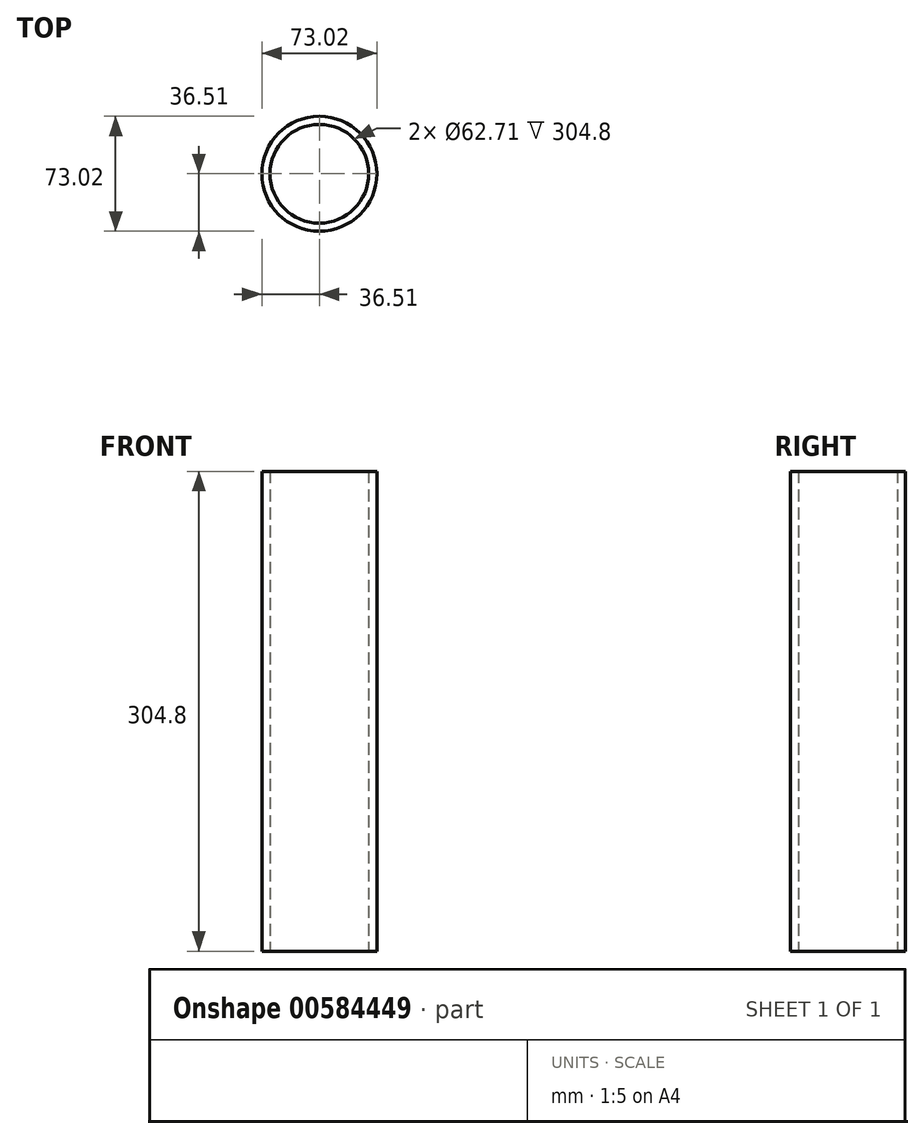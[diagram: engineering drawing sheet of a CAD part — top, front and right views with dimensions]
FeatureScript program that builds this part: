
annotation { "Feature Type Name" : "Feature", "Feature Type Description" : "" }
export const myFeature = defineFeature(function(context is Context, id is Id, definition is map)
    precondition{}
    {
        {
            var Q0;
            Q0=qCreatedBy(makeId("Top.planeOp"),FACE);
            var sketch = newSketch(context, id + "F0", { "sketchPlane" : qUnion([Q0])});
            skCircle(sketch, "E0", {"center": v(0, 0) * mm, "radius": 36.51 * mm});
            skCircle(sketch, "E1", {"center": v(0, 0) * mm, "radius": 31.36 * mm});
            skSolve(sketch);
        }
        {
            var Q0;
            Q0=qSketchRegion(id+"F0",true);
            extrude(context, id + "F1", {"entities" : qUnion([Q0]), "depth" : 304.8 * mm, "offsetDistance" : 25.4 * mm});
        }
    });
